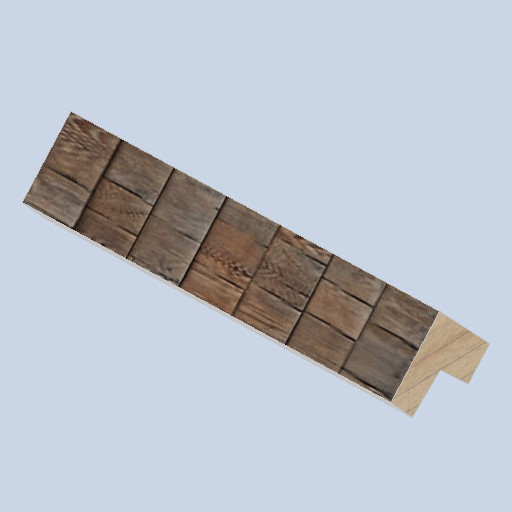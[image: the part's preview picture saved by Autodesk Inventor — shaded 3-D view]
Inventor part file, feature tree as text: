
AUTODESK INVENTOR PART (.ipt)
format: ipt  version: 2024.2 (Build 282272000, 272)  size: 519,168 bytes
history: native  units: mm
features: sketch x14, extrude x9, plane x6, projected_geometry x3, loft x1
ambient origin geometry x8: Origin, YZ Plane, XZ Plane, XY Plane, X Axis, Y Axis, Z Axis, Center Point
bodies: Solid1 (feature_tree)
feature tree (33):
  sketch  "Sketch1"  dims[d5=0.0mm d6=-7900.0mm d7=800.0mm]
  plane  "Work Plane2"
  loft  "Loft1"
  plane  "Work Plane3"
  extrude  "Extrusion1"  Depth=9000.0mm
  plane  "Work Plane4"
  sketch  "Sketch5"  dims[d12=800.0mm d13=0.0mm d14=90.0deg]
  plane  "Work Plane5"
  extrude  "Extrusion2"  Depth=9000.0mm
  plane  "Work Plane6"
  sketch  "Sketch7"  dims[d18=0.0mm d19=0.0mm d20=0.0mm]
  sketch  "Sketch8"  dims[d21=6.981317mm d22=0.0mm d23=0.0mm]
  extrude  "Extrusion3"  TaperAngle=0.0deg  [1 undecoded]
  sketch  "Sketch10"  dims[d31=120.0mm d32=120.0mm]
  extrude  "Extrusion5"  Depth=2500.0mm
  sketch  "Sketch16"  dims[d33=100.0mm d34=100.0mm]
  extrude  "Extrusion6"  TaperAngle=0.0deg  [1 undecoded]
  extrude  "Extrusion7"  TaperAngle=0.0deg  [1 undecoded]
  extrude  "Extrusion8"  Depth=1.0mm TaperAngle=0.0deg
  extrude  "Extrusion9"  Depth=120.0mm
  extrude  "Extrusion10"  Depth=100.0mm
  plane  "Work Plane1"
  sketch  "Sketch2"  dims[d8=9000.0mm d9=9000.0mm]
  sketch  "Sketch3"  dims[d10=9000.0mm d11=9000.0mm]
  sketch  "Sketch6"  dims[d15=0.0mm d16=90.0deg d17=2500.0mm]
  projected_geometry  "Projected Loop1"
  projected_geometry  "Projected Loop2"
  sketch  "Sketch9"  dims[d24=90.0deg d29=1.0mm d30=0.0mm]
  sketch  "Sketch17"  dims[d39=1100.0mm d40=0.0mm]
  sketch  "Sketch18"  dims[d41=2000.0mm d42=0.0mm]
  projected_geometry  "Projected Loop3"
  sketch  "Sketch19"  dims[d43=5000.0mm d44=0.0mm]
  sketch  "Sketch20"  dims[d45=5000.0mm d46=0.0mm d47=100.0mm d48=0.0mm d49=1100.0mm d50=0.0mm d35=500.0mm d36=0.872665mm d37=500.0mm d38=0.872665mm d51=500.0mm d52=0.872665mm]
note: 3 required parameter values undecoded (feature->parameter linkage not recoverable at this tier; creation-order binding heuristic only, values carry confidence <= 0.55)
